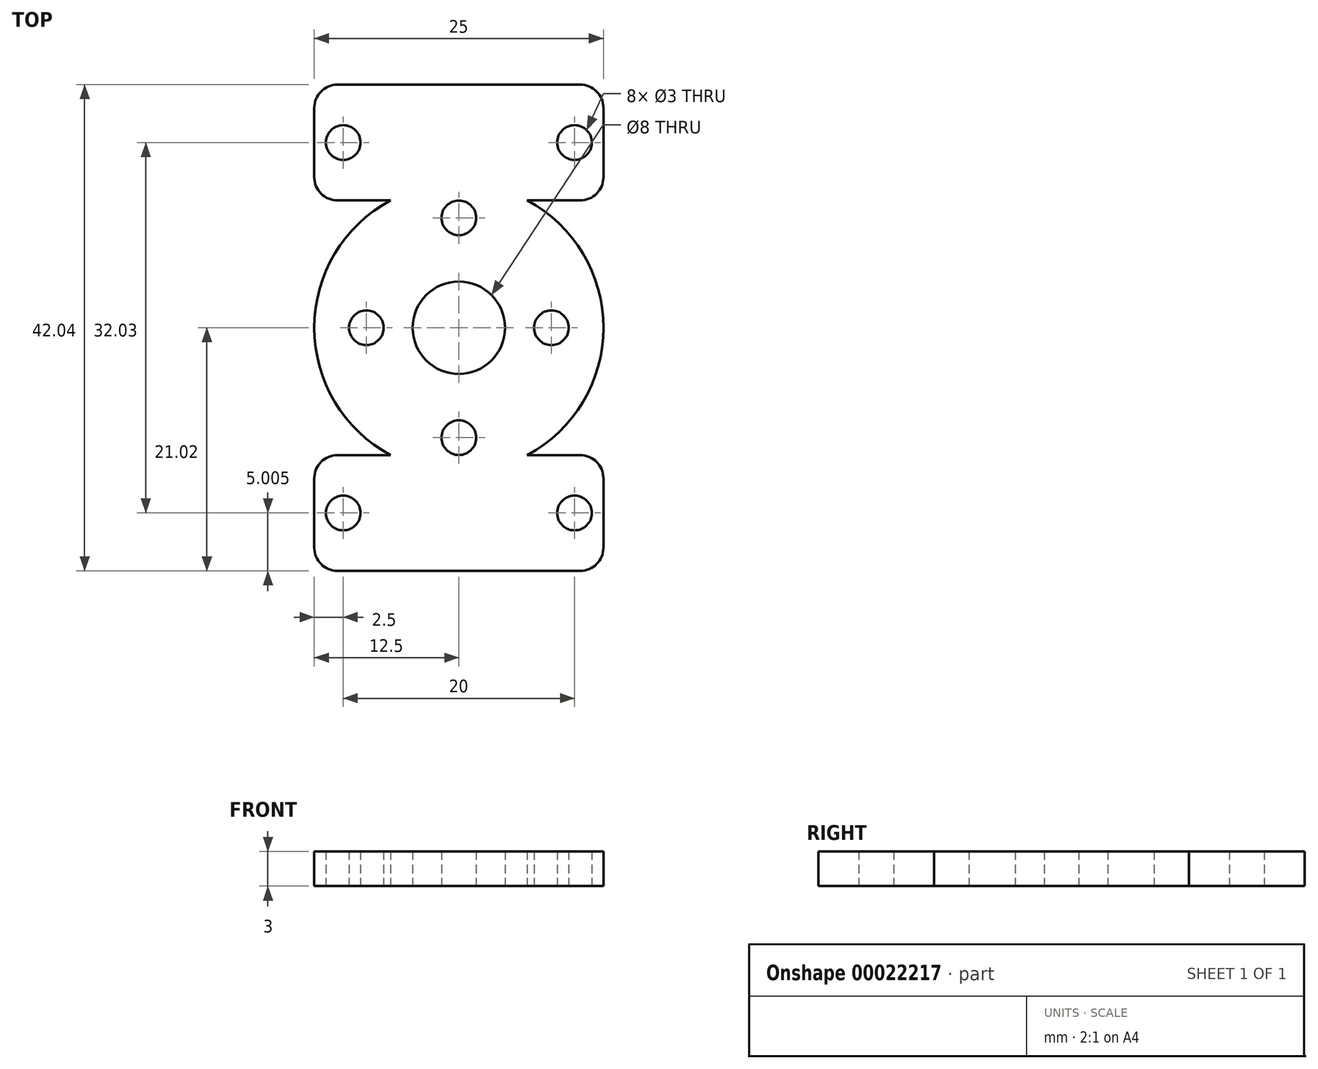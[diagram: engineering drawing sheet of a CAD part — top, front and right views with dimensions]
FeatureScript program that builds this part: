
annotation { "Feature Type Name" : "Feature", "Feature Type Description" : "" }
export const myFeature = defineFeature(function(context is Context, id is Id, definition is map)
    precondition{}
    {
        {
            var Q0;
            Q0=qCreatedBy(makeId("Top.planeOp"),FACE);
            var sketch = newSketch(context, id + "F0", { "sketchPlane" : qUnion([Q0])});
            skArc(sketch, "E0", {"start": v(5.9, -11.02) * mm, "mid": v(10.73, -6.42) * mm, "end": v(12.5, 0) * mm});
            skCircle(sketch, "E1", {"center": v(0, 9.5) * mm, "radius": 1.5 * mm});
            skLineSegment(sketch, "E2", {"start": v(-12.5, 0) * mm, "end": v(12.5, 0) * mm, "construction": true});
            skCircle(sketch, "E3.MirrorC", {"center": v(0, -9.5) * mm, "radius": 1.5 * mm});
            skCircle(sketch, "E4", {"center": v(-8, 0) * mm, "radius": 1.5 * mm});
            skLineSegment(sketch, "E5", {"start": v(0, 12.5) * mm, "end": v(0, -11) * mm, "construction": true});
            skCircle(sketch, "E6.MirrorC", {"center": v(8, 0) * mm, "radius": 1.5 * mm});
            skCircle(sketch, "E7", {"center": v(0, 0) * mm, "radius": 4 * mm});
            skLineSegment(sketch, "E8.rect.bottom", {"start": v(10.5, -21.02) * mm, "end": v(-10.5, -21.02) * mm});
            skLineSegment(sketch, "E8.rect.top", {"start": v(10.5, -11.02) * mm, "end": v(5.9, -11.02) * mm});
            skLineSegment(sketch, "E8.rect.left", {"start": v(12.5, -19.02) * mm, "end": v(12.5, -13.02) * mm});
            skLineSegment(sketch, "E8.rect.right", {"start": v(-12.5, -19.02) * mm, "end": v(-12.5, -13.02) * mm});
            skPoint(sketch, "E8.rect.middle", {"position": v(0, -16.02) * mm});
            skPoint(sketch, "E9.visualSharp", {"position": v(-12.5, -11.02) * mm});
            skArc(sketch, "E9.filletArc", {"start": v(-10.5, -11.02) * mm, "mid": v(-11.91, -11.6) * mm, "end": v(-12.5, -13.02) * mm});
            skPoint(sketch, "E10.visualSharp", {"position": v(-12.5, -21.02) * mm});
            skArc(sketch, "E10.filletArc", {"start": v(-12.5, -19.02) * mm, "mid": v(-11.91, -20.43) * mm, "end": v(-10.5, -21.02) * mm});
            skPoint(sketch, "E11.visualSharp", {"position": v(12.5, -21.02) * mm});
            skArc(sketch, "E11.filletArc", {"start": v(10.5, -21.02) * mm, "mid": v(11.91, -20.43) * mm, "end": v(12.5, -19.02) * mm});
            skPoint(sketch, "E12.visualSharp", {"position": v(12.5, -11.02) * mm});
            skArc(sketch, "E12.filletArc", {"start": v(12.5, -13.02) * mm, "mid": v(11.91, -11.6) * mm, "end": v(10.5, -11.02) * mm});
            skLineSegment(sketch, "E13.trimOffspring", {"start": v(-5.9, -11.02) * mm, "end": v(-10.5, -11.02) * mm});
            skCircle(sketch, "E14", {"center": v(-10, -16.02) * mm, "radius": 1.5 * mm});
            skLineSegment(sketch, "E15", {"start": v(0, -11) * mm, "end": v(0, -21.02) * mm, "construction": true});
            skCircle(sketch, "E16.MirrorC", {"center": v(10, -16.02) * mm, "radius": 1.5 * mm});
            skArc(sketch, "E17.trimOffspring", {"start": v(-12.5, 0) * mm, "mid": v(-10.73, -6.42) * mm, "end": v(-5.9, -11.02) * mm});
            skArc(sketch, "E18.MirrorCS", {"start": v(5.9, 11.02) * mm, "mid": v(10.73, 6.42) * mm, "end": v(12.5, 0) * mm});
            skArc(sketch, "E19.MirrorCS", {"start": v(-12.5, 0) * mm, "mid": v(-10.73, 6.42) * mm, "end": v(-5.9, 11.02) * mm});
            skLineSegment(sketch, "E20.MirrorCS", {"start": v(10.5, 21.02) * mm, "end": v(-10.5, 21.02) * mm});
            skLineSegment(sketch, "E21.MirrorCS", {"start": v(10.5, 11.02) * mm, "end": v(5.9, 11.02) * mm});
            skArc(sketch, "E22.MirrorCS", {"start": v(12.5, 13.02) * mm, "mid": v(11.91, 11.6) * mm, "end": v(10.5, 11.02) * mm});
            skLineSegment(sketch, "E23.MirrorCS", {"start": v(12.5, 19.02) * mm, "end": v(12.5, 13.02) * mm});
            skArc(sketch, "E24.MirrorCS", {"start": v(10.5, 21.02) * mm, "mid": v(11.91, 20.43) * mm, "end": v(12.5, 19.02) * mm});
            skArc(sketch, "E25.MirrorCS", {"start": v(-12.5, 19.02) * mm, "mid": v(-11.91, 20.43) * mm, "end": v(-10.5, 21.02) * mm});
            skLineSegment(sketch, "E26.MirrorCS", {"start": v(-12.5, 19.02) * mm, "end": v(-12.5, 13.02) * mm});
            skArc(sketch, "E27.MirrorCS", {"start": v(-10.5, 11.02) * mm, "mid": v(-11.91, 11.6) * mm, "end": v(-12.5, 13.02) * mm});
            skLineSegment(sketch, "E28.MirrorCS", {"start": v(-5.9, 11.02) * mm, "end": v(-10.5, 11.02) * mm});
            skCircle(sketch, "E29.MirrorC", {"center": v(-10, 16.02) * mm, "radius": 1.5 * mm});
            skCircle(sketch, "E30.MirrorC", {"center": v(10, 16.02) * mm, "radius": 1.5 * mm});
            skSolve(sketch);
        }
        {
            var Q0;
            Q0=makeQuery(id+"F0.imprint","IMPRINT",FACE,{"disambiguationData":[TD([[makeQuery(id+"F0.imprint","IMPRINT",EDGE,{"derivedFrom":sQuery(id+"F0.wireOp",EDGE,"E0")}),1.0]])]});
            extrude(context, id + "F1", {"entities" : qUnion([Q0]), "depth" : 3 * mm});
        }
    });
